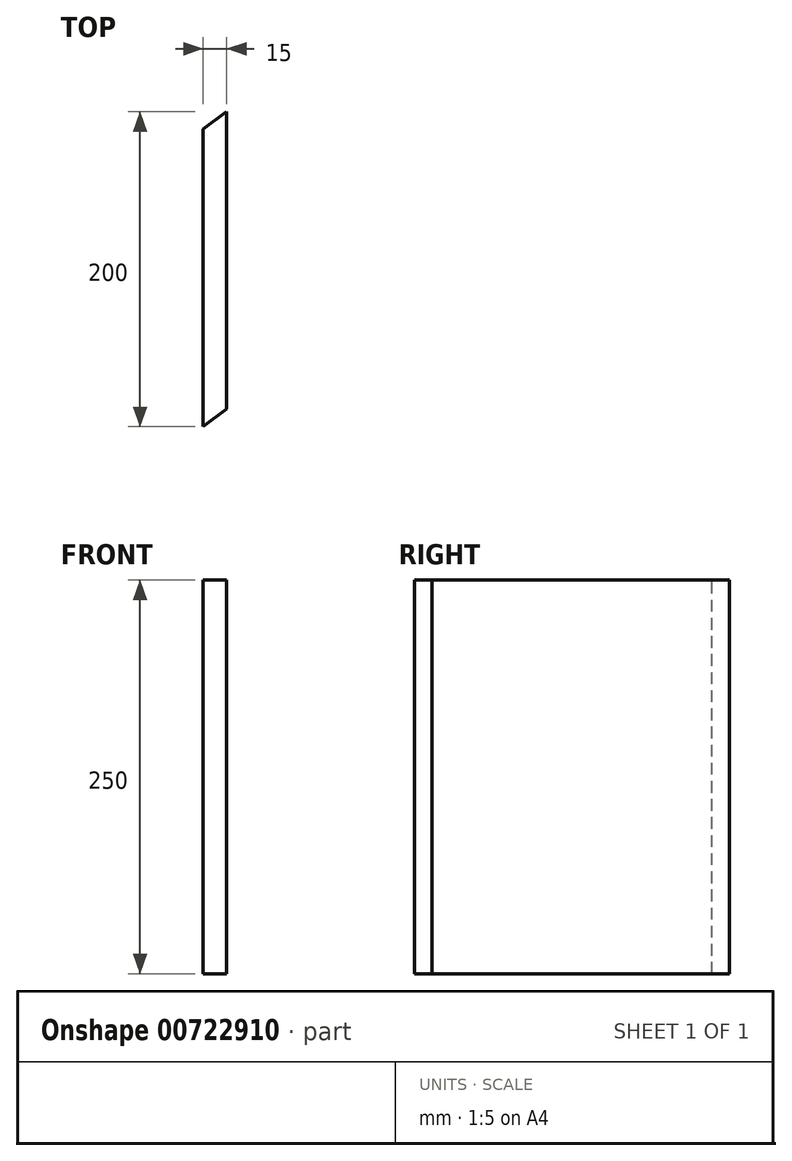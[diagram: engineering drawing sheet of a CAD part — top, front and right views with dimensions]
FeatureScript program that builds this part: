
annotation { "Feature Type Name" : "Feature", "Feature Type Description" : "" }
export const myFeature = defineFeature(function(context is Context, id is Id, definition is map)
    precondition{}
    {
        {
            var Q0;
            Q0=qCreatedBy(makeId("Right.planeOp"),FACE);
            var sketch = newSketch(context, id + "F0", { "sketchPlane" : qUnion([Q0])});
            skLineSegment(sketch, "E0.bottom", {"start": v(100, 125) * mm, "end": v(-100, 125) * mm});
            skLineSegment(sketch, "E0.top", {"start": v(100, -125) * mm, "end": v(-100, -125) * mm});
            skLineSegment(sketch, "E0.left", {"start": v(100, 125) * mm, "end": v(100, -125) * mm});
            skLineSegment(sketch, "E0.right", {"start": v(-100, 125) * mm, "end": v(-100, -125) * mm});
            skPoint(sketch, "E0.middle", {"position": v(0, 0) * mm});
            skSolve(sketch);
        }
        {
            var Q0;
            Q0=makeQuery(id+"F0.imprint","IMPRINT",FACE,{"disambiguationData":[TD([[makeQuery(id+"F0.imprint","IMPRINT",EDGE,{"derivedFrom":sQuery(id+"F0.wireOp",EDGE,"E0.bottom")}),1.0]])]});
            extrude(context, id + "F1", {"entities" : qUnion([Q0]), "depth" : 15 * mm, "offsetDistance" : 25 * mm});
        }
        {
            var Q0;
            Q0=makeQuery(id+"F1.opExtrude","SWEPT_FACE",FACE,{"disambiguationData":[OSD([sQuery(id+"F0.wireOp",EDGE,"E0.bottom")])]});
            var sketch = newSketch(context, id + "F2", { "sketchPlane" : qUnion([Q0])});
            skLineSegment(sketch, "E1", {"start": v(0, -100) * mm, "end": v(15, -88.9) * mm});
            skLineSegment(sketch, "E2", {"start": v(15, 100) * mm, "end": v(0, 88.9) * mm});
            skSolve(sketch);
        }
        {
            var Q0;
            {var subQ0=sQuery(id+"F2.wireOp",EDGE,"E2");Q0=makeQuery(id+"F2.imprint","IMPRINT",FACE,{"disambiguationData":[TD([[makeQuery(id+"F2.imprint","IMPRINT",EDGE,{"derivedFrom":subQ0}),-1.0]])]});}
            var Q1;
            {var subQ0=sQuery(id+"F2.wireOp",EDGE,"E1");Q1=makeQuery(id+"F2.imprint","IMPRINT",FACE,{"disambiguationData":[TD([[makeQuery(id+"F2.imprint","IMPRINT",EDGE,{"derivedFrom":subQ0}),-1.0]])]});}
            extrude(context, id + "F3", {"entities" : qUnion([Q0, Q1]), "operationType" : NewBodyOperationType.REMOVE, "oppositeDirection" : true, "depth" : 999 * mm, "offsetDistance" : 25 * mm});
        }
    });
